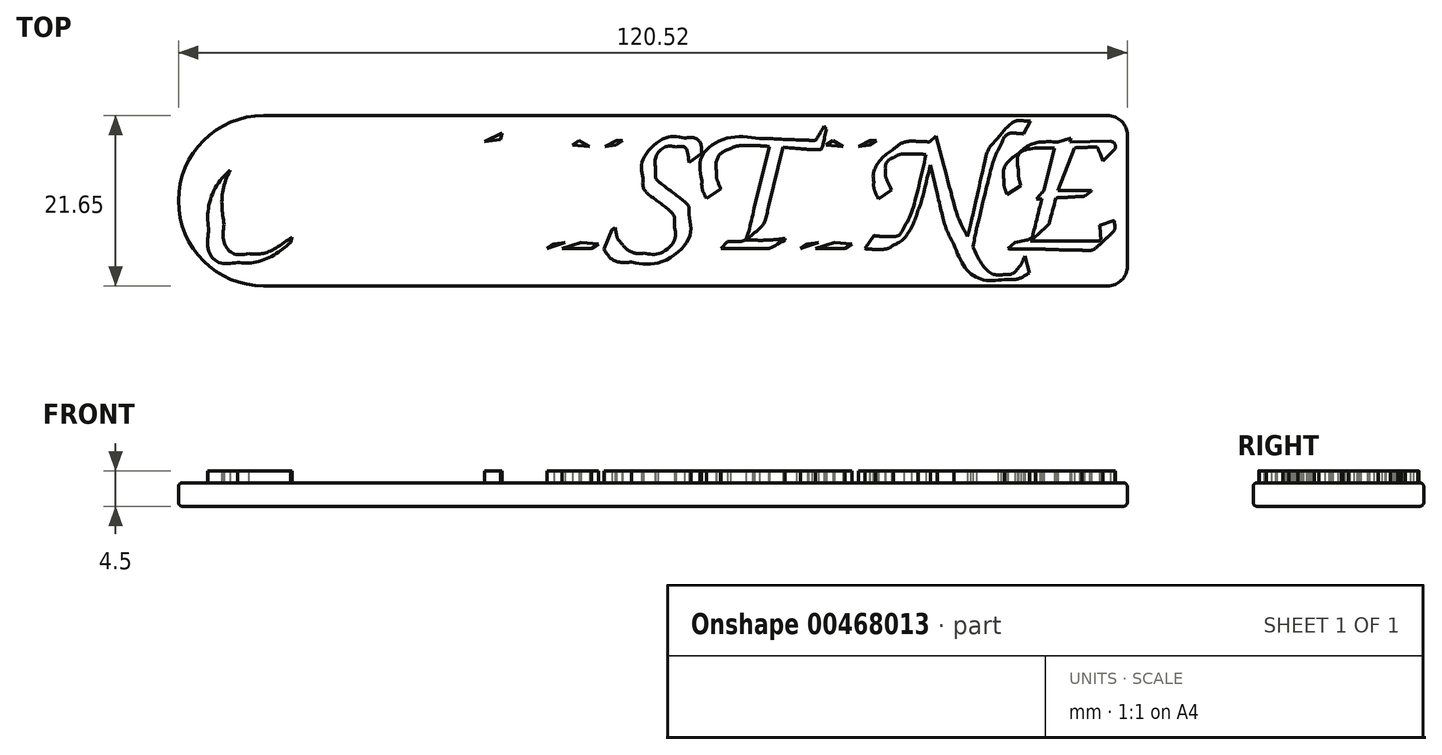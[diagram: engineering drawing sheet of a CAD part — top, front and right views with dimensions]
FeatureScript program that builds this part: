
annotation { "Feature Type Name" : "Feature", "Feature Type Description" : "" }
export const myFeature = defineFeature(function(context is Context, id is Id, definition is map)
    precondition{}
    {
        {
            var Q0;
            Q0=qCreatedBy(makeId("Top.planeOp"),FACE);
            var sketch = newSketch(context, id + "F0", { "sketchPlane" : qUnion([Q0])});
            skFitSpline(sketch, "E0", {"points": [v(-94.05, -9.34) * mm, v(-98.46, -12.36) * mm, v(-101.73, -13.6) * mm, v(-105.09, -13.6) * mm]});
            skFitSpline(sketch, "E1", {"points": [v(-105.09, -13.6) * mm, v(-108.88, -13.6) * mm, v(-111.28, -10.73) * mm, v(-111.28, -6.17) * mm]});
            skFitSpline(sketch, "E2", {"points": [v(-111.28, -6.17) * mm, v(-111.28, 3.82) * mm, v(-104.22, 13.75) * mm, v(-97.12, 13.75) * mm]});
            skFitSpline(sketch, "E3", {"points": [v(-97.12, 13.75) * mm, v(-94.24, 13.75) * mm, v(-92.8, 11.98) * mm, v(-92.51, 8.18) * mm]});
            skFitSpline(sketch, "E4", {"points": [v(-88.96, 11.2) * mm, v(-89.4, 14.52) * mm, v(-91.12, 16) * mm, v(-94.58, 16) * mm]});
            skFitSpline(sketch, "E5", {"points": [v(-94.58, 16) * mm, v(-98.75, 16) * mm, v(-103.6, 13.56) * mm, v(-107.82, 9.34) * mm]});
            skFitSpline(sketch, "E6", {"points": [v(-107.82, 9.34) * mm, v(-112.48, 4.68) * mm, v(-115.22, -1.7) * mm, v(-115.22, -7.94) * mm]});
            skFitSpline(sketch, "E7", {"points": [v(-115.22, -7.94) * mm, v(-115.22, -12.89) * mm, v(-112.48, -15.86) * mm, v(-107.87, -15.86) * mm]});
            skFitSpline(sketch, "E8", {"points": [v(-107.87, -15.86) * mm, v(-103.74, -15.86) * mm, v(-98.51, -13.9) * mm, v(-94.38, -10.78) * mm]});
            skLineSegment(sketch, "E9", {"start": v(-92.51, 8.18) * mm, "end": v(-88.96, 11.2) * mm});
            skLineSegment(sketch, "E10", {"start": v(-88.96, 11.2) * mm, "end": v(-92.51, 8.18) * mm});
            skFitSpline(sketch, "E11", {"points": [v(-75.69, 3.1) * mm, v(-75.4, 4.1) * mm, v(-74.63, 6.98) * mm, v(-73.38, 11.69) * mm]});
            skFitSpline(sketch, "E12", {"points": [v(-73.38, 11.69) * mm, v(-73.34, 11.88) * mm, v(-73.2, 12.55) * mm, v(-73, 13.46) * mm]});
            skLineSegment(sketch, "E13", {"start": v(-94.38, -10.78) * mm, "end": v(-94.05, -9.34) * mm});
            skLineSegment(sketch, "E14", {"start": v(-94.05, -9.34) * mm, "end": v(-94.38, -10.78) * mm});
            skFitSpline(sketch, "E15", {"points": [v(-71.13, 15.05) * mm, v(-72.38, 15.1) * mm, v(-73.24, 15.14) * mm, v(-73.91, 15.14) * mm]});
            skFitSpline(sketch, "E16", {"points": [v(-73.91, 15.14) * mm, v(-78.62, 15.14) * mm, v(-81.88, 14.28) * mm, v(-84.47, 12.36) * mm]});
            skFitSpline(sketch, "E17", {"points": [v(-84.47, 12.36) * mm, v(-87.06, 10.44) * mm, v(-88.22, 8.23) * mm, v(-88.22, 5.2) * mm]});
            skFitSpline(sketch, "E18", {"points": [v(-88.22, 5.2) * mm, v(-88.22, 4.49) * mm, v(-88.12, 3.96) * mm, v(-87.78, 2.8) * mm]});
            skLineSegment(sketch, "E19", {"start": v(-73, 13.46) * mm, "end": v(-71.13, 15.05) * mm});
            skLineSegment(sketch, "E20", {"start": v(-71.13, 15.05) * mm, "end": v(-73, 13.46) * mm});
            skFitSpline(sketch, "E21", {"points": [v(-84.18, 4) * mm, v(-84.62, 5.54) * mm, v(-84.76, 6.26) * mm, v(-84.76, 7.32) * mm]});
            skFitSpline(sketch, "E22", {"points": [v(-84.76, 7.32) * mm, v(-84.76, 9.96) * mm, v(-83.66, 11.93) * mm, v(-81.69, 12.74) * mm]});
            skFitSpline(sketch, "E23", {"points": [v(-81.69, 12.74) * mm, v(-80.54, 13.22) * mm, v(-79.38, 13.37) * mm, v(-76.4, 13.37) * mm]});
            skFitSpline(sketch, "E24", {"points": [v(-76.4, 13.37) * mm, v(-77.13, 10.97) * mm, v(-77.18, 10.82) * mm, v(-79.14, 3) * mm]});
            skLineSegment(sketch, "E25", {"start": v(-87.78, 2.8) * mm, "end": v(-84.18, 4) * mm});
            skLineSegment(sketch, "E26", {"start": v(-84.18, 4) * mm, "end": v(-87.78, 2.8) * mm});
            skFitSpline(sketch, "E27", {"points": [v(-79.62, 1.08) * mm, v(-81.93, -7.85) * mm, v(-82.98, -9.14) * mm, v(-88.12, -9.14) * mm]});
            skFitSpline(sketch, "E28", {"points": [v(-88.12, -9.14) * mm, v(-88.8, -9.14) * mm, v(-89.42, -9.14) * mm, v(-90.66, -9.05) * mm]});
            skLineSegment(sketch, "E29", {"start": v(-79.14, 3) * mm, "end": v(-80.87, 1.18) * mm});
            skLineSegment(sketch, "E30", {"start": v(-80.87, 1.18) * mm, "end": v(-79.62, 1.08) * mm});
            skLineSegment(sketch, "E31", {"start": v(-79.62, 1.08) * mm, "end": v(-79.14, 3) * mm});
            skFitSpline(sketch, "E32", {"points": [v(-92.92, -12.17) * mm, v(-91.86, -12.31) * mm, v(-91.38, -12.36) * mm, v(-90.57, -12.36) * mm]});
            skFitSpline(sketch, "E33", {"points": [v(-90.57, -12.36) * mm, v(-89.03, -12.36) * mm, v(-87.83, -12.22) * mm, v(-86.87, -11.88) * mm]});
            skFitSpline(sketch, "E34", {"points": [v(-86.87, -11.88) * mm, v(-85.43, -11.45) * mm, v(-82.98, -9.53) * mm, v(-80.49, -6.94) * mm]});
            skFitSpline(sketch, "E35", {"points": [v(-80.49, -6.94) * mm, v(-77.94, -4.3) * mm, v(-77.8, -4) * mm, v(-76.22, 0.98) * mm]});
            skFitSpline(sketch, "E36", {"points": [v(-76.22, 0.98) * mm, v(-70.26, 1.37) * mm, v(-68.54, 1.46) * mm, v(-65.85, 1.51) * mm]});
            skFitSpline(sketch, "E37", {"points": [v(-65.85, 1.51) * mm, v(-66.09, 0.5) * mm, v(-66.28, -0.17) * mm, v(-66.33, -0.46) * mm]});
            skFitSpline(sketch, "E38", {"points": [v(-66.33, -0.46) * mm, v(-68.34, -7.9) * mm, v(-69.11, -11.11) * mm, v(-69.11, -11.88) * mm]});
            skFitSpline(sketch, "E39", {"points": [v(-69.11, -11.88) * mm, v(-69.11, -12.4) * mm, v(-68.63, -12.89) * mm, v(-68.06, -12.89) * mm]});
            skFitSpline(sketch, "E40", {"points": [v(-68.06, -12.89) * mm, v(-67.72, -12.89) * mm, v(-67.24, -12.8) * mm, v(-66.71, -12.65) * mm]});
            skFitSpline(sketch, "E41", {"points": [v(-66.71, -12.65) * mm, v(-65.46, -12.31) * mm, v(-65.22, -12.26) * mm, v(-59.46, -11.2) * mm]});
            skLineSegment(sketch, "E42", {"start": v(-90.66, -9.05) * mm, "end": v(-92.92, -12.17) * mm});
            skLineSegment(sketch, "E43", {"start": v(-92.92, -12.17) * mm, "end": v(-90.66, -9.05) * mm});
            skFitSpline(sketch, "E44", {"points": [v(-58.6, -10) * mm, v(-61.2, -10.25) * mm, v(-61.96, -10.3) * mm, v(-63.11, -10.3) * mm]});
            skFitSpline(sketch, "E45", {"points": [v(-63.11, -10.3) * mm, v(-64.12, -10.3) * mm, v(-64.7, -9.82) * mm, v(-64.7, -9) * mm]});
            skFitSpline(sketch, "E46", {"points": [v(-64.7, -9) * mm, v(-64.7, -7.51) * mm, v(-64.7, -7.51) * mm, v(-62.34, 1.56) * mm]});
            skFitSpline(sketch, "E47", {"points": [v(-62.34, 1.56) * mm, v(-61.48, 4.87) * mm, v(-59.75, 11.06) * mm, v(-58.98, 13.46) * mm]});
            skFitSpline(sketch, "E48", {"points": [v(-58.98, 13.46) * mm, v(-57.93, 16.82) * mm, v(-57.11, 17.69) * mm, v(-55.1, 17.69) * mm]});
            skFitSpline(sketch, "E49", {"points": [v(-55.1, 17.69) * mm, v(-54.14, 17.69) * mm, v(-53.6, 17.6) * mm, v(-52.55, 17.2) * mm]});
            skLineSegment(sketch, "E50", {"start": v(-59.46, -11.2) * mm, "end": v(-58.6, -10) * mm});
            skLineSegment(sketch, "E51", {"start": v(-58.6, -10) * mm, "end": v(-59.46, -11.2) * mm});
            skFitSpline(sketch, "E52", {"points": [v(-50.92, 19.85) * mm, v(-51.83, 20.14) * mm, v(-52.22, 20.18) * mm, v(-53.08, 20.18) * mm]});
            skFitSpline(sketch, "E53", {"points": [v(-53.08, 20.18) * mm, v(-55.1, 20.18) * mm, v(-57.2, 18.84) * mm, v(-60.33, 15.53) * mm]});
            skFitSpline(sketch, "E54", {"points": [v(-60.33, 15.53) * mm, v(-62.25, 13.46) * mm, v(-62.92, 12.22) * mm, v(-63.74, 9.24) * mm]});
            skLineSegment(sketch, "E55", {"start": v(-52.55, 17.2) * mm, "end": v(-50.92, 19.85) * mm});
            skLineSegment(sketch, "E56", {"start": v(-50.92, 19.85) * mm, "end": v(-52.55, 17.2) * mm});
            skFitSpline(sketch, "E57", {"points": [v(-65.03, 4.58) * mm, v(-65.03, 4.54) * mm, v(-65.27, 3.72) * mm, v(-65.46, 3.1) * mm]});
            skLineSegment(sketch, "E58", {"start": v(-63.74, 9.24) * mm, "end": v(-65.03, 4.58) * mm});
            skLineSegment(sketch, "E59", {"start": v(-65.03, 4.58) * mm, "end": v(-63.74, 9.24) * mm});
            skFitSpline(sketch, "E60", {"points": [v(-60.05, -12.31) * mm, v(-57.51, -12.36) * mm, v(-57.51, -12.36) * mm, v(-57.22, -12.36) * mm]});
            skFitSpline(sketch, "E61", {"points": [v(-57.22, -12.36) * mm, v(-54.73, -12.36) * mm, v(-50.4, -12.26) * mm, v(-48.97, -12.17) * mm]});
            skLineSegment(sketch, "E62", {"start": v(-65.46, 3.1) * mm, "end": v(-75.69, 3.1) * mm});
            skLineSegment(sketch, "E63", {"start": v(-75.69, 3.1) * mm, "end": v(-65.46, 3.1) * mm});
            skFitSpline(sketch, "E64", {"points": [v(-45.41, -10.34) * mm, v(-47.2, -10.3) * mm, v(-47.62, -10.3) * mm, v(-51.75, -10.2) * mm]});
            skFitSpline(sketch, "E65", {"points": [v(-51.75, -10.2) * mm, v(-46.33, -4.78) * mm, v(-46.04, -4.34) * mm, v(-44.5, 1.75) * mm]});
            skFitSpline(sketch, "E66", {"points": [v(-44.4, 1.8) * mm, v(-43.88, 1.85) * mm, v(-43.6, 1.42) * mm, v(-43.3, 0.22) * mm]});
            skFitSpline(sketch, "E67", {"points": [v(-43.3, 0.22) * mm, v(-41.48, -7.8) * mm, v(-39.9, -12.36) * mm, v(-37.93, -15.29) * mm]});
            skFitSpline(sketch, "E68", {"points": [v(-37.93, -15.29) * mm, v(-35.86, -18.36) * mm, v(-33.03, -19.85) * mm, v(-29.24, -19.85) * mm]});
            skFitSpline(sketch, "E69", {"points": [v(-29.24, -19.85) * mm, v(-26.55, -19.85) * mm, v(-24.92, -19.27) * mm, v(-22.23, -17.3) * mm]});
            skLineSegment(sketch, "E70", {"start": v(-48.97, -12.17) * mm, "end": v(-45.41, -10.34) * mm});
            skLineSegment(sketch, "E71", {"start": v(-45.41, -10.34) * mm, "end": v(-48.97, -12.17) * mm});
            skFitSpline(sketch, "E72", {"points": [v(-24.58, -14.38) * mm, v(-26.12, -17.2) * mm, v(-27.46, -18.31) * mm, v(-29.33, -18.31) * mm]});
            skFitSpline(sketch, "E73", {"points": [v(-29.33, -18.31) * mm, v(-31.6, -18.31) * mm, v(-33.75, -15.91) * mm, v(-35.72, -11.16) * mm]});
            skFitSpline(sketch, "E74", {"points": [v(-35.72, -11.16) * mm, v(-36.97, -8.18) * mm, v(-38.45, -3.72) * mm, v(-40.42, 2.52) * mm]});
            skFitSpline(sketch, "E75", {"points": [v(-40.42, 2.52) * mm, v(-37.69, 3.38) * mm, v(-36.58, 3.91) * mm, v(-35.1, 4.87) * mm]});
            skFitSpline(sketch, "E76", {"points": [v(-35.1, 4.87) * mm, v(-32.84, 6.4) * mm, v(-31.54, 8.62) * mm, v(-31.54, 10.92) * mm]});
            skFitSpline(sketch, "E77", {"points": [v(-31.54, 10.92) * mm, v(-31.54, 13.9) * mm, v(-33.94, 15.53) * mm, v(-38.31, 15.53) * mm]});
            skFitSpline(sketch, "E78", {"points": [v(-38.31, 15.53) * mm, v(-38.89, 15.53) * mm, v(-40.09, 15.48) * mm, v(-41.1, 15.43) * mm]});
            skLineSegment(sketch, "E79", {"start": v(-22.23, -17.3) * mm, "end": v(-24.58, -14.38) * mm});
            skLineSegment(sketch, "E80", {"start": v(-24.58, -14.38) * mm, "end": v(-22.23, -17.3) * mm});
            skFitSpline(sketch, "E81", {"points": [v(-45.08, 14.9) * mm, v(-52.95, 13.56) * mm, v(-57.13, 9.91) * mm, v(-57.13, 4.3) * mm]});
            skFitSpline(sketch, "E82", {"points": [v(-57.13, 4.3) * mm, v(-57.13, 3.05) * mm, v(-56.98, 2.23) * mm, v(-56.45, 0.46) * mm]});
            skLineSegment(sketch, "E83", {"start": v(-41.1, 15.43) * mm, "end": v(-40.71, 16.97) * mm});
            skLineSegment(sketch, "E84", {"start": v(-40.71, 16.97) * mm, "end": v(-45.08, 14.9) * mm});
            skLineSegment(sketch, "E85", {"start": v(-45.08, 14.9) * mm, "end": v(-41.1, 15.43) * mm});
            skFitSpline(sketch, "E86", {"points": [v(-52.42, 2.52) * mm, v(-52.8, 4.15) * mm, v(-52.95, 4.97) * mm, v(-52.95, 6.07) * mm]});
            skFitSpline(sketch, "E87", {"points": [v(-52.95, 6.07) * mm, v(-52.95, 8.38) * mm, v(-52.23, 10.2) * mm, v(-50.74, 11.6) * mm]});
            skFitSpline(sketch, "E88", {"points": [v(-50.74, 11.6) * mm, v(-49.4, 12.8) * mm, v(-48.05, 13.32) * mm, v(-44.98, 13.7) * mm]});
            skLineSegment(sketch, "E89", {"start": v(-56.45, 0.46) * mm, "end": v(-52.42, 2.52) * mm});
            skLineSegment(sketch, "E90", {"start": v(-52.42, 2.52) * mm, "end": v(-56.45, 0.46) * mm});
            skFitSpline(sketch, "E91", {"points": [v(-45.41, 11.98) * mm, v(-45.6, 11.2) * mm, v(-45.9, 10.1) * mm, v(-46.23, 8.62) * mm]});
            skLineSegment(sketch, "E92", {"start": v(-44.98, 13.7) * mm, "end": v(-45.41, 11.98) * mm});
            skLineSegment(sketch, "E93", {"start": v(-45.41, 11.98) * mm, "end": v(-44.98, 13.7) * mm});
            skFitSpline(sketch, "E94", {"points": [v(-48.63, -0.89) * mm, v(-50.65, -9) * mm, v(-51.94, -10.25) * mm, v(-58.18, -10.2) * mm]});
            skLineSegment(sketch, "E95", {"start": v(-46.23, 8.62) * mm, "end": v(-48.63, -0.89) * mm});
            skLineSegment(sketch, "E96", {"start": v(-48.63, -0.89) * mm, "end": v(-46.23, 8.62) * mm});
            skLineSegment(sketch, "E97", {"start": v(-58.18, -10.2) * mm, "end": v(-60.05, -12.31) * mm});
            skLineSegment(sketch, "E98", {"start": v(-60.05, -12.31) * mm, "end": v(-58.18, -10.2) * mm});
            skFitSpline(sketch, "E99", {"points": [v(-39.94, 14.09) * mm, v(-36.97, 14.09) * mm, v(-35.72, 12.98) * mm, v(-35.72, 10.34) * mm]});
            skFitSpline(sketch, "E100", {"points": [v(-35.72, 10.34) * mm, v(-35.72, 7.94) * mm, v(-37.01, 5.64) * mm, v(-39.03, 4.4) * mm]});
            skFitSpline(sketch, "E101", {"points": [v(-39.03, 4.4) * mm, v(-40.47, 3.53) * mm, v(-41.62, 3.2) * mm, v(-44.21, 2.86) * mm]});
            skLineSegment(sketch, "E102", {"start": v(-41.43, 14.09) * mm, "end": v(-39.94, 14.09) * mm});
            skLineSegment(sketch, "E103", {"start": v(-39.94, 14.09) * mm, "end": v(-41.43, 14.09) * mm});
            skFitSpline(sketch, "E104", {"points": [v(-29.2, -12.36) * mm, v(-26.09, -12.31) * mm, v(-26.09, -12.31) * mm, v(-25.42, -12.31) * mm]});
            skLineSegment(sketch, "E105", {"start": v(-44.21, 2.86) * mm, "end": v(-41.43, 14.09) * mm});
            skLineSegment(sketch, "E106", {"start": v(-41.43, 14.09) * mm, "end": v(-44.21, 2.86) * mm});
            skFitSpline(sketch, "E107", {"points": [v(-20.67, -10.82) * mm, v(-19.75, -6.6) * mm, v(-16.73, 5.4) * mm, v(-14.47, 13.66) * mm]});
            skLineSegment(sketch, "E108", {"start": v(-25.42, -12.31) * mm, "end": v(-17.93, -12.36) * mm});
            skLineSegment(sketch, "E109", {"start": v(-17.93, -12.36) * mm, "end": v(-16.2, -11.16) * mm});
            skLineSegment(sketch, "E110", {"start": v(-16.2, -11.16) * mm, "end": v(-20.67, -10.82) * mm});
            skLineSegment(sketch, "E111", {"start": v(-20.67, -10.82) * mm, "end": v(-25.42, -12.31) * mm});
            skFitSpline(sketch, "E112", {"points": [v(-11.64, 15.14) * mm, v(-16.54, 15.1) * mm, v(-16.54, 15.1) * mm, v(-17.35, 15.1) * mm]});
            skFitSpline(sketch, "E113", {"points": [v(-17.35, 15.1) * mm, v(-18.12, 15.1) * mm, v(-18.31, 15.1) * mm, v(-21.05, 15.14) * mm]});
            skLineSegment(sketch, "E114", {"start": v(-14.47, 13.66) * mm, "end": v(-11.69, 13.94) * mm});
            skLineSegment(sketch, "E115", {"start": v(-11.69, 13.94) * mm, "end": v(-10, 15.14) * mm});
            skLineSegment(sketch, "E116", {"start": v(-10, 15.14) * mm, "end": v(-11.64, 15.14) * mm});
            skLineSegment(sketch, "E117", {"start": v(-11.64, 15.14) * mm, "end": v(-14.47, 13.66) * mm});
            skFitSpline(sketch, "E118", {"points": [v(-18.4, 13.66) * mm, v(-18.8, 11.88) * mm, v(-19.08, 10.68) * mm, v(-19.13, 10.44) * mm]});
            skLineSegment(sketch, "E119", {"start": v(-21.05, 15.14) * mm, "end": v(-22.73, 13.94) * mm});
            skLineSegment(sketch, "E120", {"start": v(-22.73, 13.94) * mm, "end": v(-18.4, 13.66) * mm});
            skLineSegment(sketch, "E121", {"start": v(-18.4, 13.66) * mm, "end": v(-21.05, 15.14) * mm});
            skFitSpline(sketch, "E122", {"points": [v(-20.14, 6.5) * mm, v(-23.16, -5.35) * mm, v(-23.69, -7.46) * mm, v(-23.93, -8.28) * mm]});
            skFitSpline(sketch, "E123", {"points": [v(-23.93, -8.28) * mm, v(-24.03, -8.57) * mm, v(-24.31, -9.67) * mm, v(-24.65, -10.82) * mm]});
            skLineSegment(sketch, "E124", {"start": v(-19.13, 10.44) * mm, "end": v(-20.14, 6.5) * mm});
            skLineSegment(sketch, "E125", {"start": v(-20.14, 6.5) * mm, "end": v(-19.13, 10.44) * mm});
            skLineSegment(sketch, "E126", {"start": v(-24.65, -10.82) * mm, "end": v(-27.48, -11.16) * mm});
            skLineSegment(sketch, "E127", {"start": v(-27.48, -11.16) * mm, "end": v(-29.2, -12.36) * mm});
            skLineSegment(sketch, "E128", {"start": v(-29.2, -12.36) * mm, "end": v(-24.65, -10.82) * mm});
            skFitSpline(sketch, "E129", {"points": [v(-14.82, -12.46) * mm, v(-13.14, -14.71) * mm, v(-10.88, -15.77) * mm, v(-7.76, -15.77) * mm]});
            skFitSpline(sketch, "E130", {"points": [v(-7.76, -15.77) * mm, v(-0.42, -15.77) * mm, v(6.78, -9.77) * mm, v(6.78, -3.67) * mm]});
            skFitSpline(sketch, "E131", {"points": [v(6.78, -3.67) * mm, v(6.78, -1.7) * mm, v(6.02, -0.7) * mm, v(2.46, 2.09) * mm]});
            skFitSpline(sketch, "E132", {"points": [v(2.46, 2.09) * mm, v(-1.04, 4.82) * mm, v(-1.62, 5.64) * mm, v(-1.62, 7.7) * mm]});
            skFitSpline(sketch, "E133", {"points": [v(-1.62, 7.7) * mm, v(-1.62, 10.82) * mm, v(0.74, 13.51) * mm, v(3.57, 13.51) * mm]});
            skFitSpline(sketch, "E134", {"points": [v(3.57, 13.51) * mm, v(5.58, 13.51) * mm, v(6.3, 12.65) * mm, v(6.83, 9.58) * mm]});
            skLineSegment(sketch, "E135", {"start": v(-12.7, -7.46) * mm, "end": v(-14.82, -12.46) * mm});
            skLineSegment(sketch, "E136", {"start": v(-14.82, -12.46) * mm, "end": v(-12.7, -7.46) * mm});
            skFitSpline(sketch, "E137", {"points": [v(10, 11.83) * mm, v(9.71, 14.47) * mm, v(8.27, 15.77) * mm, v(5.73, 15.77) * mm]});
            skFitSpline(sketch, "E138", {"points": [v(5.73, 15.77) * mm, v(0.78, 15.77) * mm, v(-4.83, 10.3) * mm, v(-4.83, 5.54) * mm]});
            skFitSpline(sketch, "E139", {"points": [v(-4.83, 5.54) * mm, v(-4.83, 3.38) * mm, v(-3.82, 1.8) * mm, v(-1.04, -0.36) * mm]});
            skFitSpline(sketch, "E140", {"points": [v(-1.04, -0.36) * mm, v(2.22, -2.95) * mm, v(3.09, -4.25) * mm, v(3.09, -6.46) * mm]});
            skFitSpline(sketch, "E141", {"points": [v(3.09, -6.46) * mm, v(3.09, -10.2) * mm, v(-0.51, -13.51) * mm, v(-4.69, -13.51) * mm]});
            skFitSpline(sketch, "E142", {"points": [v(-4.69, -13.51) * mm, v(-6.75, -13.51) * mm, v(-8.86, -12.6) * mm, v(-10.16, -11.16) * mm]});
            skFitSpline(sketch, "E143", {"points": [v(-10.16, -11.16) * mm, v(-11.17, -10.06) * mm, v(-11.55, -9.05) * mm, v(-11.94, -6.94) * mm]});
            skLineSegment(sketch, "E144", {"start": v(6.83, 9.58) * mm, "end": v(10, 11.83) * mm});
            skLineSegment(sketch, "E145", {"start": v(10, 11.83) * mm, "end": v(6.83, 9.58) * mm});
            skFitSpline(sketch, "E146", {"points": [v(14.99, -12.36) * mm, v(26.56, -12.36) * mm, v(27.28, -12.26) * mm, v(31.17, -10.1) * mm]});
            skLineSegment(sketch, "E147", {"start": v(-11.94, -6.94) * mm, "end": v(-12.7, -7.46) * mm});
            skLineSegment(sketch, "E148", {"start": v(-12.7, -7.46) * mm, "end": v(-11.94, -6.94) * mm});
            skFitSpline(sketch, "E149", {"points": [v(31.26, -9.72) * mm, v(29.15, -10) * mm, v(26.08, -10.2) * mm, v(23.49, -10.2) * mm]});
            skFitSpline(sketch, "E150", {"points": [v(23.49, -10.2) * mm, v(23.1, -10.2) * mm, v(22.29, -10.15) * mm, v(21.28, -10.1) * mm]});
            skFitSpline(sketch, "E151", {"points": [v(21.28, -10.1) * mm, v(24.97, -6.98) * mm, v(26.17, -5.26) * mm, v(26.99, -1.6) * mm]});
            skLineSegment(sketch, "E152", {"start": v(31.17, -10.1) * mm, "end": v(31.26, -9.72) * mm});
            skLineSegment(sketch, "E153", {"start": v(31.26, -9.72) * mm, "end": v(31.17, -10.1) * mm});
            skFitSpline(sketch, "E154", {"points": [v(30.73, 13.42) * mm, v(37.02, 12.89) * mm, v(37.07, 12.89) * mm, v(38.03, 12.89) * mm]});
            skFitSpline(sketch, "E155", {"points": [v(38.03, 12.89) * mm, v(40.29, 12.89) * mm, v(40.62, 13.32) * mm, v(41.77, 18.07) * mm]});
            skLineSegment(sketch, "E156", {"start": v(26.99, -1.6) * mm, "end": v(30.73, 13.42) * mm});
            skLineSegment(sketch, "E157", {"start": v(30.73, 13.42) * mm, "end": v(26.99, -1.6) * mm});
            skFitSpline(sketch, "E158", {"points": [v(41.15, 18.8) * mm, v(39.18, 15.43) * mm, v(38.94, 15.2) * mm, v(37.21, 15.2) * mm]});
            skFitSpline(sketch, "E159", {"points": [v(37.21, 15.2) * mm, v(36.78, 15.2) * mm, v(35.68, 15.24) * mm, v(34.19, 15.29) * mm]});
            skFitSpline(sketch, "E160", {"points": [v(34.19, 15.29) * mm, v(27.13, 15.62) * mm, v(26.27, 15.67) * mm, v(24.73, 15.67) * mm]});
            skFitSpline(sketch, "E161", {"points": [v(24.73, 15.67) * mm, v(16.33, 15.67) * mm, v(10.1, 11.11) * mm, v(10.1, 4.97) * mm]});
            skFitSpline(sketch, "E162", {"points": [v(10.1, 4.97) * mm, v(10.1, 3.43) * mm, v(10.43, 2.09) * mm, v(11.3, 0.4) * mm]});
            skLineSegment(sketch, "E163", {"start": v(41.77, 18.07) * mm, "end": v(41.15, 18.8) * mm});
            skLineSegment(sketch, "E164", {"start": v(41.15, 18.8) * mm, "end": v(41.77, 18.07) * mm});
            skFitSpline(sketch, "E165", {"points": [v(14.9, 2.76) * mm, v(13.98, 5.11) * mm, v(13.79, 5.83) * mm, v(13.79, 7.18) * mm]});
            skFitSpline(sketch, "E166", {"points": [v(13.79, 7.18) * mm, v(13.79, 9.86) * mm, v(15.04, 11.93) * mm, v(17.39, 13.03) * mm]});
            skFitSpline(sketch, "E167", {"points": [v(17.39, 13.03) * mm, v(18.59, 13.6) * mm, v(20.37, 13.85) * mm, v(22.9, 13.85) * mm]});
            skFitSpline(sketch, "E168", {"points": [v(22.9, 13.85) * mm, v(23.92, 13.85) * mm, v(24.88, 13.8) * mm, v(27.28, 13.6) * mm]});
            skLineSegment(sketch, "E169", {"start": v(11.3, 0.4) * mm, "end": v(14.9, 2.76) * mm});
            skLineSegment(sketch, "E170", {"start": v(14.9, 2.76) * mm, "end": v(11.3, 0.4) * mm});
            skFitSpline(sketch, "E171", {"points": [v(23.39, -2.04) * mm, v(21.66, -9.1) * mm, v(20.75, -10.3) * mm, v(16.67, -10.49) * mm]});
            skLineSegment(sketch, "E172", {"start": v(27.28, 13.6) * mm, "end": v(23.39, -2.04) * mm});
            skLineSegment(sketch, "E173", {"start": v(23.39, -2.04) * mm, "end": v(27.28, 13.6) * mm});
            skFitSpline(sketch, "E174", {"points": [v(35.2, -12.36) * mm, v(38.32, -12.31) * mm, v(38.32, -12.31) * mm, v(38.99, -12.31) * mm]});
            skLineSegment(sketch, "E175", {"start": v(16.67, -10.49) * mm, "end": v(14.99, -12.36) * mm});
            skLineSegment(sketch, "E176", {"start": v(14.99, -12.36) * mm, "end": v(16.67, -10.49) * mm});
            skFitSpline(sketch, "E177", {"points": [v(43.74, -10.82) * mm, v(44.65, -6.6) * mm, v(47.68, 5.4) * mm, v(49.93, 13.66) * mm]});
            skLineSegment(sketch, "E178", {"start": v(38.99, -12.31) * mm, "end": v(46.48, -12.36) * mm});
            skLineSegment(sketch, "E179", {"start": v(46.48, -12.36) * mm, "end": v(48.2, -11.16) * mm});
            skLineSegment(sketch, "E180", {"start": v(48.2, -11.16) * mm, "end": v(43.74, -10.82) * mm});
            skLineSegment(sketch, "E181", {"start": v(43.74, -10.82) * mm, "end": v(38.99, -12.31) * mm});
            skFitSpline(sketch, "E182", {"points": [v(52.77, 15.14) * mm, v(47.87, 15.1) * mm, v(47.87, 15.1) * mm, v(47.05, 15.1) * mm]});
            skFitSpline(sketch, "E183", {"points": [v(47.05, 15.1) * mm, v(46.29, 15.1) * mm, v(46.1, 15.1) * mm, v(43.36, 15.14) * mm]});
            skLineSegment(sketch, "E184", {"start": v(49.93, 13.66) * mm, "end": v(52.72, 13.94) * mm});
            skLineSegment(sketch, "E185", {"start": v(52.72, 13.94) * mm, "end": v(54.4, 15.14) * mm});
            skLineSegment(sketch, "E186", {"start": v(54.4, 15.14) * mm, "end": v(52.77, 15.14) * mm});
            skLineSegment(sketch, "E187", {"start": v(52.77, 15.14) * mm, "end": v(49.93, 13.66) * mm});
            skFitSpline(sketch, "E188", {"points": [v(46, 13.66) * mm, v(45.61, 11.88) * mm, v(45.33, 10.68) * mm, v(45.28, 10.44) * mm]});
            skLineSegment(sketch, "E189", {"start": v(43.36, 15.14) * mm, "end": v(41.68, 13.94) * mm});
            skLineSegment(sketch, "E190", {"start": v(41.68, 13.94) * mm, "end": v(46, 13.66) * mm});
            skLineSegment(sketch, "E191", {"start": v(46, 13.66) * mm, "end": v(43.36, 15.14) * mm});
            skFitSpline(sketch, "E192", {"points": [v(44.27, 6.5) * mm, v(41.25, -5.35) * mm, v(40.72, -7.46) * mm, v(40.48, -8.28) * mm]});
            skFitSpline(sketch, "E193", {"points": [v(40.48, -8.28) * mm, v(40.38, -8.57) * mm, v(40.1, -9.67) * mm, v(39.76, -10.82) * mm]});
            skLineSegment(sketch, "E194", {"start": v(45.28, 10.44) * mm, "end": v(44.27, 6.5) * mm});
            skLineSegment(sketch, "E195", {"start": v(44.27, 6.5) * mm, "end": v(45.28, 10.44) * mm});
            skFitSpline(sketch, "E196", {"points": [v(51.51, -12.36) * mm, v(52.8, -12.46) * mm, v(53.48, -12.5) * mm, v(54.15, -12.5) * mm]});
            skFitSpline(sketch, "E197", {"points": [v(54.15, -12.5) * mm, v(56.21, -12.5) * mm, v(57.51, -12.22) * mm, v(58.76, -11.45) * mm]});
            skFitSpline(sketch, "E198", {"points": [v(58.76, -11.45) * mm, v(61.11, -10.06) * mm, v(63.51, -6.6) * mm, v(65.05, -2.57) * mm]});
            skFitSpline(sketch, "E199", {"points": [v(65.05, -2.57) * mm, v(65.81, -0.5) * mm, v(66.1, 0.55) * mm, v(68.17, 8.86) * mm]});
            skLineSegment(sketch, "E200", {"start": v(39.76, -10.82) * mm, "end": v(36.93, -11.16) * mm});
            skLineSegment(sketch, "E201", {"start": v(36.93, -11.16) * mm, "end": v(35.2, -12.36) * mm});
            skLineSegment(sketch, "E202", {"start": v(35.2, -12.36) * mm, "end": v(39.76, -10.82) * mm});
            skFitSpline(sketch, "E203", {"points": [v(69.94, 1.42) * mm, v(71.33, -4.54) * mm, v(72.49, -8.04) * mm, v(74.12, -11.3) * mm]});
            skFitSpline(sketch, "E204", {"points": [v(74.12, -11.3) * mm, v(77.05, -17.26) * mm, v(81.27, -20.18) * mm, v(86.93, -20.18) * mm]});
            skFitSpline(sketch, "E205", {"points": [v(86.93, -20.18) * mm, v(89.38, -20.18) * mm, v(91.11, -19.75) * mm, v(93.27, -18.5) * mm]});
            skLineSegment(sketch, "E206", {"start": v(68.17, 8.86) * mm, "end": v(69.94, 1.42) * mm});
            skLineSegment(sketch, "E207", {"start": v(69.94, 1.42) * mm, "end": v(68.17, 8.86) * mm});
            skFitSpline(sketch, "E208", {"points": [v(92.12, -14.23) * mm, v(91.45, -15.82) * mm, v(91.11, -16.49) * mm, v(90.49, -17.2) * mm]});
            skFitSpline(sketch, "E209", {"points": [v(90.49, -17.2) * mm, v(89.62, -18.26) * mm, v(88.42, -18.89) * mm, v(87.22, -18.89) * mm]});
            skFitSpline(sketch, "E210", {"points": [v(87.22, -18.89) * mm, v(84.2, -18.89) * mm, v(81.41, -16.54) * mm, v(78.97, -11.88) * mm]});
            skFitSpline(sketch, "E211", {"points": [v(78.97, -11.88) * mm, v(79.78, -7.75) * mm, v(80.21, -5.88) * mm, v(81.41, -0.84) * mm]});
            skFitSpline(sketch, "E212", {"points": [v(81.41, -0.84) * mm, v(83.48, 7.51) * mm, v(84.53, 10.97) * mm, v(86.07, 14.14) * mm]});
            skFitSpline(sketch, "E213", {"points": [v(86.07, 14.14) * mm, v(87.08, 16.15) * mm, v(88.23, 16.92) * mm, v(90.44, 16.92) * mm]});
            skFitSpline(sketch, "E214", {"points": [v(90.44, 16.92) * mm, v(90.77, 16.92) * mm, v(91.06, 16.92) * mm, v(91.73, 16.82) * mm]});
            skLineSegment(sketch, "E215", {"start": v(93.27, -18.5) * mm, "end": v(92.12, -14.23) * mm});
            skLineSegment(sketch, "E216", {"start": v(92.12, -14.23) * mm, "end": v(93.27, -18.5) * mm});
            skFitSpline(sketch, "E217", {"points": [v(93.51, 20.04) * mm, v(92.93, 20.09) * mm, v(92.4, 20.14) * mm, v(92.02, 20.14) * mm]});
            skFitSpline(sketch, "E218", {"points": [v(92.02, 20.14) * mm, v(90, 20.14) * mm, v(87.85, 18.74) * mm, v(85.35, 15.82) * mm]});
            skFitSpline(sketch, "E219", {"points": [v(85.35, 15.82) * mm, v(83.05, 13.13) * mm, v(82.18, 10.68) * mm, v(79.83, 0.31) * mm]});
            skFitSpline(sketch, "E220", {"points": [v(79.83, 0.31) * mm, v(79.35, -1.94) * mm, v(78.82, -4.2) * mm, v(78.3, -6.5) * mm]});
            skFitSpline(sketch, "E221", {"points": [v(78.3, -6.5) * mm, v(78.25, -6.74) * mm, v(78, -7.75) * mm, v(77.57, -9.24) * mm]});
            skFitSpline(sketch, "E222", {"points": [v(77.57, -9.24) * mm, v(75.27, -4.63) * mm, v(74.65, -2.76) * mm, v(69.56, 16.25) * mm]});
            skLineSegment(sketch, "E223", {"start": v(91.73, 16.82) * mm, "end": v(93.51, 20.04) * mm});
            skLineSegment(sketch, "E224", {"start": v(93.51, 20.04) * mm, "end": v(91.73, 16.82) * mm});
            skFitSpline(sketch, "E225", {"points": [v(67.93, 14.76) * mm, v(66.77, 14.86) * mm, v(66.15, 14.9) * mm, v(65.29, 14.9) * mm]});
            skFitSpline(sketch, "E226", {"points": [v(65.29, 14.9) * mm, v(62.4, 14.9) * mm, v(60.68, 14.38) * mm, v(58.95, 13.03) * mm]});
            skFitSpline(sketch, "E227", {"points": [v(58.95, 13.03) * mm, v(55.88, 10.63) * mm, v(53.77, 7.18) * mm, v(53.77, 4.54) * mm]});
            skFitSpline(sketch, "E228", {"points": [v(53.77, 4.54) * mm, v(53.77, 3.34) * mm, v(54.1, 2.09) * mm, v(54.97, 0.31) * mm]});
            skLineSegment(sketch, "E229", {"start": v(69.56, 16.25) * mm, "end": v(67.93, 14.76) * mm});
            skLineSegment(sketch, "E230", {"start": v(67.93, 14.76) * mm, "end": v(69.56, 16.25) * mm});
            skFitSpline(sketch, "E231", {"points": [v(58.28, 2.57) * mm, v(57.08, 5.11) * mm, v(56.74, 6.22) * mm, v(56.74, 7.42) * mm]});
            skFitSpline(sketch, "E232", {"points": [v(56.74, 7.42) * mm, v(56.74, 8.86) * mm, v(57.56, 10.15) * mm, v(58.9, 10.87) * mm]});
            skFitSpline(sketch, "E233", {"points": [v(58.9, 10.87) * mm, v(60.05, 11.5) * mm, v(61.2, 11.69) * mm, v(63.37, 11.69) * mm]});
            skFitSpline(sketch, "E234", {"points": [v(63.37, 11.69) * mm, v(64.37, 11.69) * mm, v(65.24, 11.69) * mm, v(67.06, 11.6) * mm]});
            skFitSpline(sketch, "E235", {"points": [v(67.06, 11.6) * mm, v(64.8, 1.94) * mm, v(62.98, -4.1) * mm, v(61.4, -6.94) * mm]});
            skFitSpline(sketch, "E236", {"points": [v(61.4, -6.94) * mm, v(60.4, -8.71) * mm, v(59.33, -9.24) * mm, v(56.8, -9.24) * mm]});
            skFitSpline(sketch, "E237", {"points": [v(56.8, -9.24) * mm, v(55.88, -9.24) * mm, v(55.16, -9.2) * mm, v(53.81, -9.05) * mm]});
            skLineSegment(sketch, "E238", {"start": v(54.97, 0.31) * mm, "end": v(58.28, 2.57) * mm});
            skLineSegment(sketch, "E239", {"start": v(58.28, 2.57) * mm, "end": v(54.97, 0.31) * mm});
            skLineSegment(sketch, "E240", {"start": v(53.81, -9.05) * mm, "end": v(51.51, -12.36) * mm});
            skLineSegment(sketch, "E241", {"start": v(51.51, -12.36) * mm, "end": v(53.81, -9.05) * mm});
            skFitSpline(sketch, "E242", {"points": [v(104.75, 13.27) * mm, v(106.77, 13.37) * mm, v(108.26, 13.42) * mm, v(108.54, 13.42) * mm]});
            skFitSpline(sketch, "E243", {"points": [v(108.54, 13.42) * mm, v(110.42, 13.42) * mm, v(110.75, 13.08) * mm, v(112.05, 9.91) * mm]});
            skLineSegment(sketch, "E244", {"start": v(100.53, 2.38) * mm, "end": v(103.26, 13.27) * mm});
            skLineSegment(sketch, "E245", {"start": v(103.26, 13.27) * mm, "end": v(104.75, 13.27) * mm});
            skLineSegment(sketch, "E246", {"start": v(104.75, 13.27) * mm, "end": v(100.53, 2.38) * mm});
            skFitSpline(sketch, "E247", {"points": [v(115.22, 13.08) * mm, v(115.07, 14.14) * mm, v(114.69, 14.66) * mm, v(113.87, 14.95) * mm]});
            skLineSegment(sketch, "E248", {"start": v(112.05, 9.91) * mm, "end": v(115.22, 13.08) * mm});
            skLineSegment(sketch, "E249", {"start": v(115.22, 13.08) * mm, "end": v(112.05, 9.91) * mm});
            skFitSpline(sketch, "E250", {"points": [v(100.53, 14.76) * mm, v(95.92, 14.71) * mm, v(93, 13.8) * mm, v(90.26, 11.64) * mm]});
            skFitSpline(sketch, "E251", {"points": [v(90.26, 11.64) * mm, v(87.86, 9.72) * mm, v(86.8, 7.8) * mm, v(86.8, 5.3) * mm]});
            skFitSpline(sketch, "E252", {"points": [v(86.8, 5.3) * mm, v(86.8, 4.06) * mm, v(87, 3.1) * mm, v(87.66, 1.42) * mm]});
            skLineSegment(sketch, "E253", {"start": v(113.87, 14.95) * mm, "end": v(103.6, 14.76) * mm});
            skLineSegment(sketch, "E254", {"start": v(103.6, 14.76) * mm, "end": v(103.89, 15.77) * mm});
            skLineSegment(sketch, "E255", {"start": v(103.89, 15.77) * mm, "end": v(100.53, 14.76) * mm});
            skLineSegment(sketch, "E256", {"start": v(100.53, 14.76) * mm, "end": v(113.87, 14.95) * mm});
            skFitSpline(sketch, "E257", {"points": [v(91.12, 3.72) * mm, v(90.69, 5.26) * mm, v(90.5, 6.5) * mm, v(90.5, 7.7) * mm]});
            skFitSpline(sketch, "E258", {"points": [v(90.5, 7.7) * mm, v(90.5, 11.45) * mm, v(93.18, 12.98) * mm, v(99.71, 13.18) * mm]});
            skLineSegment(sketch, "E259", {"start": v(87.66, 1.42) * mm, "end": v(91.12, 3.72) * mm});
            skLineSegment(sketch, "E260", {"start": v(91.12, 3.72) * mm, "end": v(87.66, 1.42) * mm});
            skFitSpline(sketch, "E261", {"points": [v(97.02, 2.38) * mm, v(96.2, 1.56) * mm, v(95.97, 1.27) * mm, v(95.15, 0.31) * mm]});
            skLineSegment(sketch, "E262", {"start": v(99.71, 13.18) * mm, "end": v(97.02, 2.38) * mm});
            skLineSegment(sketch, "E263", {"start": v(97.02, 2.38) * mm, "end": v(99.71, 13.18) * mm});
            skFitSpline(sketch, "E264", {"points": [v(96.5, 0.31) * mm, v(96.3, -0.4) * mm, v(96.16, -1.03) * mm, v(95.97, -1.6) * mm]});
            skFitSpline(sketch, "E265", {"points": [v(95.97, -1.6) * mm, v(94.14, -9) * mm, v(93.62, -9.82) * mm, v(89.68, -10.78) * mm]});
            skLineSegment(sketch, "E266", {"start": v(95.15, 0.31) * mm, "end": v(96.5, 0.31) * mm});
            skLineSegment(sketch, "E267", {"start": v(96.5, 0.31) * mm, "end": v(95.15, 0.31) * mm});
            skFitSpline(sketch, "E268", {"points": [v(87.86, -12.36) * mm, v(89.2, -12.4) * mm, v(90.2, -12.4) * mm, v(90.54, -12.4) * mm]});
            skLineSegment(sketch, "E269", {"start": v(89.68, -10.78) * mm, "end": v(87.86, -12.36) * mm});
            skLineSegment(sketch, "E270", {"start": v(87.86, -12.36) * mm, "end": v(89.68, -10.78) * mm});
            skFitSpline(sketch, "E271", {"points": [v(94.86, -12.46) * mm, v(96.3, -12.46) * mm, v(97.6, -12.5) * mm, v(98.7, -12.55) * mm]});
            skFitSpline(sketch, "E272", {"points": [v(98.7, -12.55) * mm, v(104.51, -12.74) * mm, v(104.56, -12.74) * mm, v(106.62, -12.74) * mm]});
            skFitSpline(sketch, "E273", {"points": [v(106.62, -12.74) * mm, v(109.12, -12.74) * mm, v(109.8, -12.46) * mm, v(111.95, -10.49) * mm]});
            skFitSpline(sketch, "E274", {"points": [v(111.95, -10.49) * mm, v(114.16, -8.52) * mm, v(114.98, -7.37) * mm, v(114.98, -6.26) * mm]});
            skFitSpline(sketch, "E275", {"points": [v(114.98, -6.26) * mm, v(114.98, -6.02) * mm, v(114.93, -5.64) * mm, v(114.78, -5.16) * mm]});
            skLineSegment(sketch, "E276", {"start": v(90.54, -12.4) * mm, "end": v(94.86, -12.46) * mm});
            skLineSegment(sketch, "E277", {"start": v(94.86, -12.46) * mm, "end": v(90.54, -12.4) * mm});
            skFitSpline(sketch, "E278", {"points": [v(111.14, -6.5) * mm, v(111.28, -7.51) * mm, v(111.33, -7.9) * mm, v(111.33, -8.33) * mm]});
            skFitSpline(sketch, "E279", {"points": [v(111.33, -8.33) * mm, v(111.33, -10.15) * mm, v(110.7, -10.4) * mm, v(106.1, -10.4) * mm]});
            skLineSegment(sketch, "E280", {"start": v(114.78, -5.16) * mm, "end": v(111.14, -6.5) * mm});
            skLineSegment(sketch, "E281", {"start": v(111.14, -6.5) * mm, "end": v(114.78, -5.16) * mm});
            skFitSpline(sketch, "E282", {"points": [v(93.62, -10.4) * mm, v(98.27, -6.12) * mm, v(98.32, -6.02) * mm, v(100.05, 0.55) * mm]});
            skFitSpline(sketch, "E283", {"points": [v(100.05, 0.55) * mm, v(102.5, 0.7) * mm, v(102.78, 0.7) * mm, v(103.94, 0.8) * mm]});
            skFitSpline(sketch, "E284", {"points": [v(103.94, 0.8) * mm, v(105, 0.84) * mm, v(105.71, 0.89) * mm, v(106, 0.89) * mm]});
            skFitSpline(sketch, "E285", {"points": [v(106, 0.89) * mm, v(106.2, 0.94) * mm, v(106.72, 0.94) * mm, v(107.3, 0.98) * mm]});
            skFitSpline(sketch, "E286", {"points": [v(107.3, 0.98) * mm, v(108.16, 1.6) * mm, v(108.26, 1.7) * mm, v(109.12, 2.38) * mm]});
            skLineSegment(sketch, "E287", {"start": v(106.1, -10.4) * mm, "end": v(93.62, -10.4) * mm});
            skLineSegment(sketch, "E288", {"start": v(93.62, -10.4) * mm, "end": v(106.1, -10.4) * mm});
            skLineSegment(sketch, "E289", {"start": v(109.12, 2.38) * mm, "end": v(100.53, 2.38) * mm});
            skLineSegment(sketch, "E290", {"start": v(100.53, 2.38) * mm, "end": v(109.12, 2.38) * mm});
            skLineSegment(sketch, "E291", {"start": v(-44.5, 1.75) * mm, "end": v(-44.4, 1.8) * mm});
            skSolve(sketch);
        }
        {
            var Q0;
            Q0=qCreatedBy(makeId("Top.planeOp"),FACE);
            var sketch = newSketch(context, id + "F1", { "sketchPlane" : qUnion([Q0])});
            skLineSegment(sketch, "E292.bottom", {"start": v(-101.21, 21.48) * mm, "end": v(118.18, 21.48) * mm});
            skLineSegment(sketch, "E292.top", {"start": v(-101.21, -21.83) * mm, "end": v(118.18, -21.83) * mm});
            skLineSegment(sketch, "E292.left", {"start": v(-101.21, 21.48) * mm, "end": v(-101.21, -21.83) * mm});
            skLineSegment(sketch, "E292.right", {"start": v(118.18, 21.48) * mm, "end": v(118.18, -21.83) * mm});
            skArc(sketch, "E293", {"start": v(-101.21, 21.48) * mm, "mid": v(-122.87, -0.17) * mm, "end": v(-101.21, -21.83) * mm});
            skArc(sketch, "E294", {"start": v(118.18, 21.48) * mm, "mid": v(139.84, -0.17) * mm, "end": v(118.18, -21.83) * mm});
            skArc(sketch, "E295", {"start": v(118.18, 16.7) * mm, "mid": v(135.05, -0.17) * mm, "end": v(118.18, -17.04) * mm});
            skSolve(sketch);
        }
        {
            var Q0;
            {var subQ0=sQuery(id+"F1.wireOp",EDGE,"E294");Q0=makeQuery(id+"F1.imprint","IMPRINT",FACE,{"disambiguationData":[TD([[makeQuery(id+"F1.imprint","IMPRINT",EDGE,{"derivedFrom":subQ0}),-1.0]])]});}
            var Q1;
            {var subQ2=sQuery(id+"F1.wireOp",EDGE,"E292.bottom");Q1=makeQuery(id+"F1.imprint","IMPRINT",FACE,{"disambiguationData":[TD([[makeQuery(id+"F1.imprint","IMPRINT",EDGE,{"derivedFrom":subQ2}),-1.0]])]});}
            var Q2;
            Q2=makeQuery(id+"F1.imprint","IMPRINT",FACE,{"disambiguationData":[TD([[makeQuery(id+"F1.imprint","IMPRINT",EDGE,{"derivedFrom":sQuery(id+"F1.wireOp",EDGE,"E292.left")}),-1.0]])]});
            extrude(context, id + "F2", {"entities" : qUnion([Q0, Q1, Q2]), "oppositeDirection" : true, "depth" : 6 * mm});
        }
        {
            var Q0;
            Q0=makeQuery(id+"F0.imprint","IMPRINT",FACE,{"disambiguationData":[TD([[makeQuery(id+"F0.imprint","IMPRINT",EDGE,{"derivedFrom":sQuery(id+"F0.wireOp",EDGE,"E0")}),1.0]])]});
            var Q1;
            Q1=makeQuery(id+"F0.imprint","IMPRINT",FACE,{"disambiguationData":[TD([[makeQuery(id+"F0.imprint","IMPRINT",EDGE,{"derivedFrom":sQuery(id+"F0.wireOp",EDGE,"E11")}),1.0]])]});
            var Q2;
            Q2=makeQuery(id+"F0.imprint","IMPRINT",FACE,{"disambiguationData":[TD([[makeQuery(id+"F0.imprint","IMPRINT",EDGE,{"derivedFrom":sQuery(id+"F0.wireOp",EDGE,"E60")}),1.0]])]});
            var Q3;
            Q3=makeQuery(id+"F0.imprint","IMPRINT",FACE,{"disambiguationData":[TD([[makeQuery(id+"F0.imprint","IMPRINT",EDGE,{"derivedFrom":sQuery(id+"F0.wireOp",EDGE,"E83")}),1.0]])]});
            var Q4;
            Q4=makeQuery(id+"F0.imprint","IMPRINT",FACE,{"disambiguationData":[TD([[makeQuery(id+"F0.imprint","IMPRINT",EDGE,{"derivedFrom":sQuery(id+"F0.wireOp",EDGE,"E104")}),1.0]])]});
            var Q5;
            Q5=makeQuery(id+"F0.imprint","IMPRINT",FACE,{"disambiguationData":[TD([[makeQuery(id+"F0.imprint","IMPRINT",EDGE,{"derivedFrom":sQuery(id+"F0.wireOp",EDGE,"E119")}),1.0]])]});
            var Q6;
            Q6=makeQuery(id+"F0.imprint","IMPRINT",FACE,{"disambiguationData":[TD([[makeQuery(id+"F0.imprint","IMPRINT",EDGE,{"derivedFrom":sQuery(id+"F0.wireOp",EDGE,"E114")}),1.0]])]});
            var Q7;
            Q7=makeQuery(id+"F0.imprint","IMPRINT",FACE,{"disambiguationData":[TD([[makeQuery(id+"F0.imprint","IMPRINT",EDGE,{"derivedFrom":sQuery(id+"F0.wireOp",EDGE,"E108")}),1.0]])]});
            var Q8;
            Q8=makeQuery(id+"F0.imprint","IMPRINT",FACE,{"disambiguationData":[TD([[makeQuery(id+"F0.imprint","IMPRINT",EDGE,{"derivedFrom":sQuery(id+"F0.wireOp",EDGE,"E126")}),1.0]])]});
            var Q9;
            Q9=makeQuery(id+"F0.imprint","IMPRINT",FACE,{"disambiguationData":[TD([[makeQuery(id+"F0.imprint","IMPRINT",EDGE,{"derivedFrom":sQuery(id+"F0.wireOp",EDGE,"E129")}),1.0]])]});
            var Q10;
            Q10=makeQuery(id+"F0.imprint","IMPRINT",FACE,{"disambiguationData":[TD([[makeQuery(id+"F0.imprint","IMPRINT",EDGE,{"derivedFrom":sQuery(id+"F0.wireOp",EDGE,"E146")}),1.0]])]});
            var Q11;
            Q11=makeQuery(id+"F0.imprint","IMPRINT",FACE,{"disambiguationData":[TD([[makeQuery(id+"F0.imprint","IMPRINT",EDGE,{"derivedFrom":sQuery(id+"F0.wireOp",EDGE,"E174")}),1.0]])]});
            var Q12;
            Q12=makeQuery(id+"F0.imprint","IMPRINT",FACE,{"disambiguationData":[TD([[makeQuery(id+"F0.imprint","IMPRINT",EDGE,{"derivedFrom":sQuery(id+"F0.wireOp",EDGE,"E189")}),1.0]])]});
            var Q13;
            Q13=makeQuery(id+"F0.imprint","IMPRINT",FACE,{"disambiguationData":[TD([[makeQuery(id+"F0.imprint","IMPRINT",EDGE,{"derivedFrom":sQuery(id+"F0.wireOp",EDGE,"E184")}),1.0]])]});
            var Q14;
            Q14=makeQuery(id+"F0.imprint","IMPRINT",FACE,{"disambiguationData":[TD([[makeQuery(id+"F0.imprint","IMPRINT",EDGE,{"derivedFrom":sQuery(id+"F0.wireOp",EDGE,"E200")}),1.0]])]});
            var Q15;
            Q15=makeQuery(id+"F0.imprint","IMPRINT",FACE,{"disambiguationData":[TD([[makeQuery(id+"F0.imprint","IMPRINT",EDGE,{"derivedFrom":sQuery(id+"F0.wireOp",EDGE,"E178")}),1.0]])]});
            var Q16;
            Q16=makeQuery(id+"F0.imprint","IMPRINT",FACE,{"disambiguationData":[TD([[makeQuery(id+"F0.imprint","IMPRINT",EDGE,{"derivedFrom":sQuery(id+"F0.wireOp",EDGE,"E196")}),1.0]])]});
            var Q17;
            Q17=makeQuery(id+"F0.imprint","IMPRINT",FACE,{"disambiguationData":[TD([[makeQuery(id+"F0.imprint","IMPRINT",EDGE,{"derivedFrom":sQuery(id+"F0.wireOp",EDGE,"E242")}),1.0]])]});
            var Q18;
            Q18=makeQuery(id+"F0.imprint","IMPRINT",FACE,{"disambiguationData":[TD([[makeQuery(id+"F0.imprint","IMPRINT",EDGE,{"derivedFrom":sQuery(id+"F0.wireOp",EDGE,"E244")}),-1.0]])]});
            var Q19;
            {var subQ0=sQuery(id+"F0.wireOp",EDGE,"E255");Q19=makeQuery(id+"F0.imprint","IMPRINT",FACE,{"disambiguationData":[TD([[makeQuery(id+"F0.imprint","IMPRINT",EDGE,{"derivedFrom":subQ0}),1.0]])]});}
            extrude(context, id + "F3", {"entities" : qUnion([Q0, Q1, Q2, Q3, Q4, Q5, Q6, Q7, Q8, Q9, Q10, Q11, Q12, Q13, Q14, Q15, Q16, Q17, Q18, Q19]), "operationType" : NewBodyOperationType.ADD, "depth" : 3 * mm});
        }
        {
            var Q0;
            {var subQ0=sQuery(id+"F1.wireOp",EDGE,"E295");var subQ1=sQuery(id+"F1.wireOp",EDGE,"E292.right");Q0=makeQuery(id+"F2.opExtrude","SWEPT_EDGE",EDGE,{"disambiguationData":[OSD([subQ1,subQ0]),TDD([makeQuery(id+"F1.imprint","INTERSECT",VERTEX,{"disambiguationData":[OD(0.0)],"derivedFrom":[subQ1,subQ0]})])]});}
            var Q1;
            {var subQ0=sQuery(id+"F1.wireOp",EDGE,"E295");var subQ1=sQuery(id+"F1.wireOp",EDGE,"E292.right");Q1=makeQuery(id+"F2.opExtrude","SWEPT_EDGE",EDGE,{"disambiguationData":[OSD([subQ1,subQ0]),TDD([makeQuery(id+"F1.imprint","INTERSECT",VERTEX,{"disambiguationData":[OD(1.0)],"derivedFrom":[subQ1,subQ0]})])]});}
            fillet(context, id + "F4", {"entities" : qUnion([Q0, Q1]), "radius" : 5 * mm, "tangentPropagation" : true, "allowEdgeOverflow" : false});
        }
        {
            var Q0;
            Q0=makeQuery(id+"F2.opExtrude","CAP_EDGE",EDGE,{"disambiguationData":[OSD([sQuery(id+"F1.wireOp",EDGE,"E292.bottom")])],"isStart":true});
            var Q1;
            Q1=makeQuery(id+"F2.opExtrude","CAP_EDGE",EDGE,{"disambiguationData":[OSD([sQuery(id+"F1.wireOp",EDGE,"E292.bottom")])],"isStart":false});
            fillet(context, id + "F5", {"entities" : qUnion([Q0, Q1]), "radius" : 1 * mm, "tangentPropagation" : true, "allowEdgeOverflow" : false});
        }
        {
            var Q0;
            Q0=makeQuery(id+"F2.opExtrude","SWEPT_BODY",BODY,{"disambiguationData":[OSD([sQuery(id+"F1.wireOp",EDGE,"E292.bottom"),sQuery(id+"F1.wireOp",EDGE,"E292.top"),sQuery(id+"F1.wireOp",EDGE,"E292.right"),sQuery(id+"F1.wireOp",EDGE,"E293"),sQuery(id+"F1.wireOp",EDGE,"E294"),sQuery(id+"F1.wireOp",EDGE,"E295")])]});
            var Q1;
            Q1=qCreatedBy(makeId("Origin.pointOp"),VERTEX);
            transform(context, id + "F6", {"entities" : qUnion([Q0]), "transformType" : TransformType.SCALE_UNIFORMLY, "scale" : 0.5, "scalePoint" : qUnion([Q1]), "makeCopy" : false});
        }
    });
